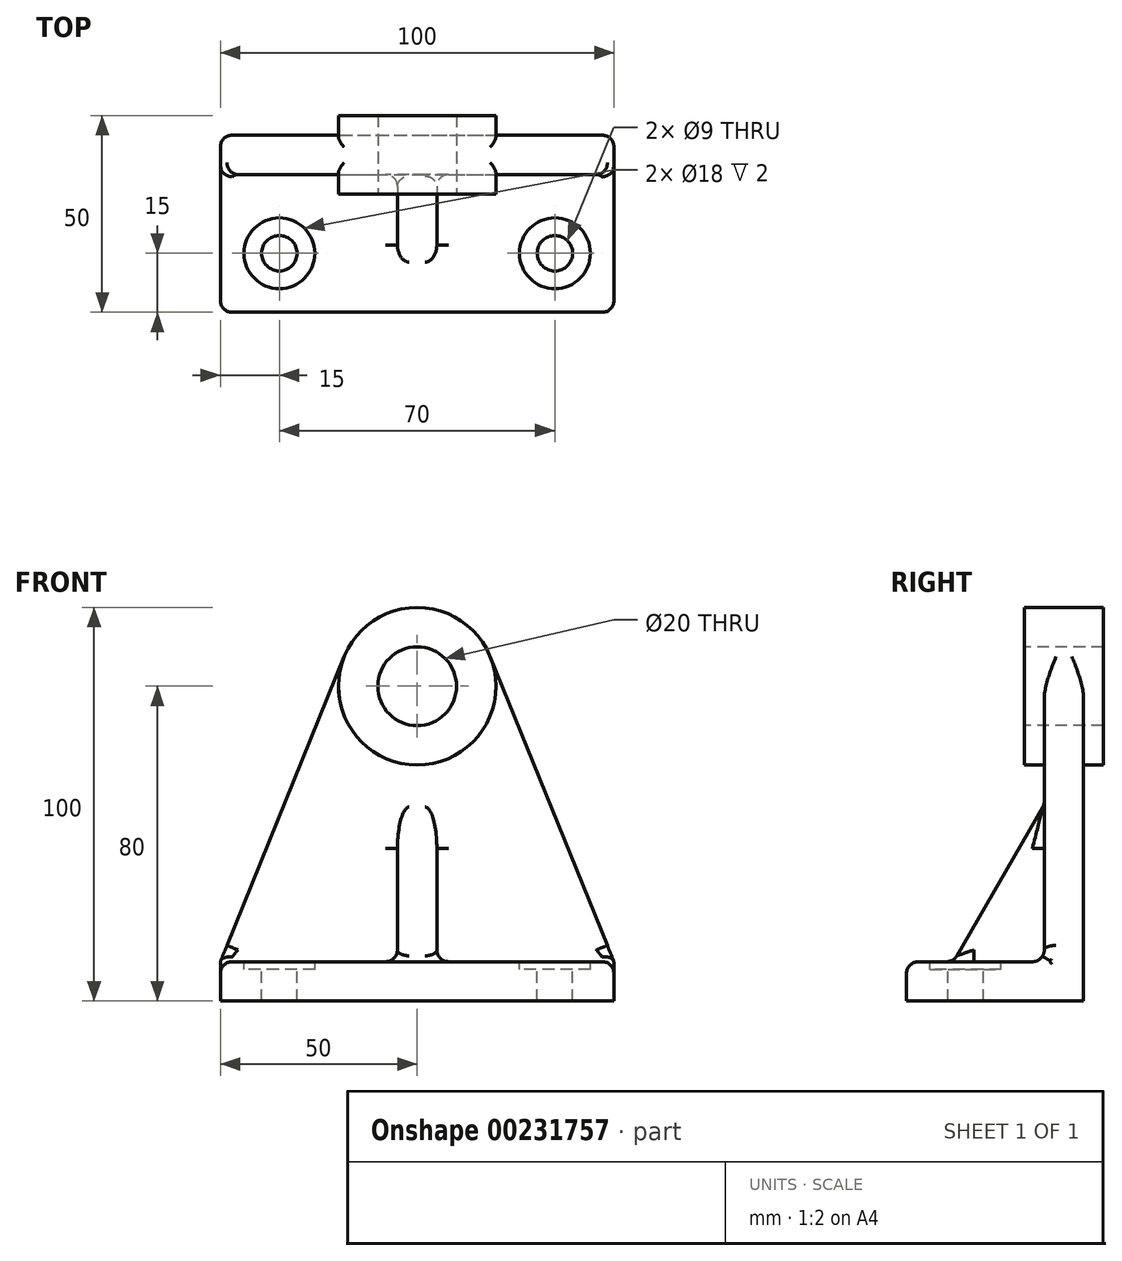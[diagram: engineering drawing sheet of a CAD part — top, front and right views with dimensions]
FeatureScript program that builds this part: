
annotation { "Feature Type Name" : "Feature", "Feature Type Description" : "" }
export const myFeature = defineFeature(function(context is Context, id is Id, definition is map)
    precondition{}
    {
        {
            var Q0;
            Q0=qCreatedBy(makeId("Front.planeOp"),FACE);
            var sketch = newSketch(context, id + "F0", { "sketchPlane" : qUnion([Q0])});
            skCircle(sketch, "E0", {"center": v(0, 80) * mm, "radius": 20 * mm, "construction": true});
            skLineSegment(sketch, "E1", {"start": v(-50, 0) * mm, "end": v(-50, 10) * mm});
            skLineSegment(sketch, "E2", {"start": v(-50, 10) * mm, "end": v(-18.53, 87.52) * mm});
            skLineSegment(sketch, "E3.MirrorCS", {"start": v(50, 10) * mm, "end": v(18.53, 87.52) * mm});
            skLineSegment(sketch, "E4.MirrorCS", {"start": v(50, 0) * mm, "end": v(50, 10) * mm});
            skLineSegment(sketch, "E5", {"start": v(-50, 0) * mm, "end": v(50, 0) * mm});
            skLineSegment(sketch, "E6", {"start": v(-18.53, 87.52) * mm, "end": v(18.53, 87.52) * mm});
            skSolve(sketch);
        }
        {
            var Q0;
            Q0 = qSketchRegion(id + "F0", true);
            extrude(context, id + "F1", {"entities" : qUnion([Q0]), "depth" : 45 * mm});
        }
        {
            var Q0;
            Q0=qCreatedBy(makeId("Right.planeOp"),FACE);
            var sketch = newSketch(context, id + "F2", { "sketchPlane" : qUnion([Q0])});
            skLineSegment(sketch, "E7.bottom", {"start": v(-55, 97.52) * mm, "end": v(-10, 97.52) * mm});
            skLineSegment(sketch, "E7.top", {"start": v(-55, 10) * mm, "end": v(-10, 10) * mm});
            skLineSegment(sketch, "E7.left", {"start": v(-55, 97.52) * mm, "end": v(-55, 10) * mm});
            skLineSegment(sketch, "E7.right", {"start": v(-10, 97.52) * mm, "end": v(-10, 10) * mm});
            skSolve(sketch);
        }
        {
            var Q0;
            Q0 = qSketchRegion(id + "F2", true);
            extrude(context, id + "F3", {"entities" : qUnion([Q0]), "operationType" : NewBodyOperationType.REMOVE, "endBound" : BoundingType.THROUGH_ALL, "oppositeDirection" : true, "depth" : 25 * mm, "hasSecondDirection" : true, "secondDirectionBound" : SecondDirectionBoundingType.THROUGH_ALL, "secondDirectionOppositeDirection" : false, "secondDirectionDepth" : 25 * mm});
        }
        {
            var Q0;
            Q0=qCreatedBy(makeId("Front.planeOp"),FACE);
            var sketch = newSketch(context, id + "F4", { "sketchPlane" : qUnion([Q0])});
            skCircle(sketch, "E8", {"center": v(0, 80) * mm, "radius": 20 * mm});
            skSolve(sketch);
        }
        {
            var Q0;
            Q0 = qSketchRegion(id + "F4", true);
            extrude(context, id + "F5", {"entities" : qUnion([Q0]), "operationType" : NewBodyOperationType.ADD, "depth" : 15 * mm, "hasSecondDirection" : true, "secondDirectionOppositeDirection" : true, "secondDirectionDepth" : 5 * mm});
        }
        {
            var Q0;
            Q0=qCreatedBy(makeId("Right.planeOp"),FACE);
            var sketch = newSketch(context, id + "F6", { "sketchPlane" : qUnion([Q0])});
            skLineSegment(sketch, "E9", {"start": v(-10, 50) * mm, "end": v(-33.1, 10) * mm});
            skLineSegment(sketch, "E10", {"start": v(-33.1, 10) * mm, "end": v(-33.1, 6) * mm});
            skLineSegment(sketch, "E11", {"start": v(-33.1, 6) * mm, "end": v(-6, 6) * mm});
            skLineSegment(sketch, "E12", {"start": v(-6, 6) * mm, "end": v(-6, 50) * mm});
            skLineSegment(sketch, "E13", {"start": v(-6, 50) * mm, "end": v(-10, 50) * mm});
            skSolve(sketch);
        }
        {
            var Q0;
            Q0 = qSketchRegion(id + "F6", true);
            extrude(context, id + "F7", {"entities" : qUnion([Q0]), "operationType" : NewBodyOperationType.ADD, "depth" : 5 * mm, "hasSecondDirection" : true, "secondDirectionOppositeDirection" : true, "secondDirectionDepth" : 5 * mm});
        }
        {
            var Q0;
            Q0=makeQuery(id+"F5.opExtrude","CAP_FACE",FACE,{"disambiguationData":[OSD([sQuery(id+"F4.wireOp",EDGE,"E8")])],"isStart":false});
            var sketch = newSketch(context, id + "F8", { "sketchPlane" : qUnion([Q0])});
            skCircle(sketch, "E14", {"center": v(0, 80) * mm, "radius": 10 * mm});
            skSolve(sketch);
        }
        {
            var Q0;
            Q0 = qSketchRegion(id + "F8", true);
            extrude(context, id + "F9", {"entities" : qUnion([Q0]), "operationType" : NewBodyOperationType.REMOVE, "endBound" : BoundingType.THROUGH_ALL, "oppositeDirection" : true, "depth" : 25 * mm});
        }
        {
            var Q0;
            Q0=makeQuery(id+"F3.boolean.opBoolean","COPY",FACE,{"derivedFrom":makeQuery(id+"F3.opExtrude","SWEPT_FACE",FACE,{"disambiguationData":[OSD([sQuery(id+"F2.wireOp",EDGE,"E7.top")])]})});
            var sketch = newSketch(context, id + "F10", { "sketchPlane" : qUnion([Q0])});
            skPoint(sketch, "E15", {"position": v(-35, -30) * mm});
            skPoint(sketch, "E16.MirrorP", {"position": v(35, -30) * mm});
            skSolve(sketch);
        }
        {
            var Q0;
            Q0=sQuery(id+"F10.wireOp",VERTEX,"E15");
            var Q1;
            Q1=sQuery(id+"F10.wireOp",VERTEX,"E16.MirrorP");
            var Q2;
            Q2=makeQuery(id+"F1.opExtrude","SWEPT_BODY",BODY,{"disambiguationData":[OSD([sQuery(id+"F0.wireOp",EDGE,"E1"),sQuery(id+"F0.wireOp",EDGE,"E2"),sQuery(id+"F0.wireOp",EDGE,"E3.MirrorCS"),sQuery(id+"F0.wireOp",EDGE,"E4.MirrorCS"),sQuery(id+"F0.wireOp",EDGE,"E5"),sQuery(id+"F0.wireOp",EDGE,"E6")])]});
            hole(context, id + "F11", {"style" : HoleStyle.C_BORE, "endStyle" : HoleEndStyle.THROUGH, "holeDiameter" : 9 * mm, "cBoreDiameter" : 18 * mm, "cBoreDepth" : 2 * mm, "locations" : qUnion([Q0, Q1]), "scope" : qUnion([Q2]), "isTappedThrough" : true});
        }
        {
            var Q0;
            Q0=makeQuery(id+"F1.opExtrude","CAP_EDGE",EDGE,{"disambiguationData":[OSD([sQuery(id+"F0.wireOp",EDGE,"E1")])],"isStart":false});
            var Q1;
            Q1=makeQuery(id+"F1.opExtrude","CAP_EDGE",EDGE,{"disambiguationData":[OSD([sQuery(id+"F0.wireOp",EDGE,"E4.MirrorCS")])],"isStart":false});
            fillet(context, id + "F12", {"entities" : qUnion([Q0, Q1]), "radius" : 3 * mm, "tangentPropagation" : true, "allowEdgeOverflow" : false});
        }
        {
            var Q0;
            Q0=makeQuery(id+"F7.opExtrude","CAP_EDGE",EDGE,{"disambiguationData":[OSD([sQuery(id+"F6.wireOp",EDGE,"E9")])],"isStart":false});
            var Q1;
            Q1=makeQuery(id+"F7.opExtrude","CAP_EDGE",EDGE,{"disambiguationData":[OSD([sQuery(id+"F6.wireOp",EDGE,"E9")])],"isStart":true});
            fillet(context, id + "F13", {"entities" : qUnion([Q0, Q1]), "radius" : 3 * mm, "tangentPropagation" : true, "allowEdgeOverflow" : false});
        }
        {
            var Q0;
            {var subQ0=sQuery(id+"F2.wireOp",EDGE,"E7.right");var subQ1=sQuery(id+"F2.wireOp",EDGE,"E7.top");Q0=makeQuery(id+"F7.boolean.opBoolean","SPLIT",EDGE,{"disambiguationData":[TD([makeQuery(id+"F1.opExtrude","SWEPT_FACE",FACE,{"disambiguationData":[OSD([sQuery(id+"F0.wireOp",EDGE,"E3.MirrorCS")])]})])],"derivedFrom":makeQuery(id+"F3.boolean.opBoolean","COPY",EDGE,{"derivedFrom":makeQuery(id+"F3.opExtrude","SWEPT_EDGE",EDGE,{"disambiguationData":[OSD([subQ1,subQ0])]})})});}
            var Q1;
            {var subQ0=sQuery(id+"F2.wireOp",EDGE,"E7.right");var subQ1=sQuery(id+"F2.wireOp",EDGE,"E7.top");Q1=makeQuery(id+"F7.boolean.opBoolean","SPLIT",EDGE,{"disambiguationData":[TD([makeQuery(id+"F1.opExtrude","SWEPT_FACE",FACE,{"disambiguationData":[OSD([sQuery(id+"F0.wireOp",EDGE,"E1")])]})])],"derivedFrom":makeQuery(id+"F3.boolean.opBoolean","COPY",EDGE,{"derivedFrom":makeQuery(id+"F3.opExtrude","SWEPT_EDGE",EDGE,{"disambiguationData":[OSD([subQ1,subQ0])]})})});}
            fillet(context, id + "F14", {"entities" : qUnion([Q0, Q1]), "radius" : 3 * mm, "tangentPropagation" : true, "allowEdgeOverflow" : false});
        }
        {
            var Q0;
            {var subQ0=sQuery(id+"F0.wireOp",EDGE,"E2");var subQ1=sQuery(id+"F0.wireOp",EDGE,"E1");Q0=makeQuery(id+"F3.boolean.opBoolean","SPLIT",EDGE,{"disambiguationData":[TD([makeQuery(id+"F1.opExtrude","CAP_FACE",FACE,{"disambiguationData":[OSD([subQ1,subQ0,sQuery(id+"F0.wireOp",EDGE,"E3.MirrorCS"),sQuery(id+"F0.wireOp",EDGE,"E4.MirrorCS"),sQuery(id+"F0.wireOp",EDGE,"E5"),sQuery(id+"F0.wireOp",EDGE,"E6")])],"isStart":true})])],"derivedFrom":makeQuery(id+"F1.opExtrude","SWEPT_EDGE",EDGE,{"disambiguationData":[OSD([subQ1,subQ0])]})});}
            var Q1;
            {var subQ0=sQuery(id+"F0.wireOp",EDGE,"E4.MirrorCS");var subQ1=sQuery(id+"F0.wireOp",EDGE,"E3.MirrorCS");Q1=makeQuery(id+"F3.boolean.opBoolean","SPLIT",EDGE,{"disambiguationData":[TD([makeQuery(id+"F1.opExtrude","CAP_FACE",FACE,{"disambiguationData":[OSD([sQuery(id+"F0.wireOp",EDGE,"E1"),sQuery(id+"F0.wireOp",EDGE,"E2"),subQ1,subQ0,sQuery(id+"F0.wireOp",EDGE,"E5"),sQuery(id+"F0.wireOp",EDGE,"E6")])],"isStart":true})])],"derivedFrom":makeQuery(id+"F1.opExtrude","SWEPT_EDGE",EDGE,{"disambiguationData":[OSD([subQ1,subQ0])]})});}
            fillet(context, id + "F15", {"entities" : qUnion([Q0, Q1]), "radius" : 3 * mm, "tangentPropagation" : true, "allowEdgeOverflow" : false});
        }
        {
            var Q0;
            Q0=makeQuery(id+"F3.boolean.opBoolean","INTERSECT",EDGE,{"derivedFrom":[makeQuery(id+"F1.opExtrude","CAP_FACE",FACE,{"disambiguationData":[OSD([sQuery(id+"F0.wireOp",EDGE,"E1"),sQuery(id+"F0.wireOp",EDGE,"E2"),sQuery(id+"F0.wireOp",EDGE,"E3.MirrorCS"),sQuery(id+"F0.wireOp",EDGE,"E4.MirrorCS"),sQuery(id+"F0.wireOp",EDGE,"E5"),sQuery(id+"F0.wireOp",EDGE,"E6")])],"isStart":false}),makeQuery(id+"F3.opExtrude","SWEPT_FACE",FACE,{"disambiguationData":[OSD([sQuery(id+"F2.wireOp",EDGE,"E7.top")])]})]});
            var Q1;
            Q1=makeQuery(id+"F3.boolean.opBoolean","INTERSECT",EDGE,{"derivedFrom":[makeQuery(id+"F1.opExtrude","SWEPT_FACE",FACE,{"disambiguationData":[OSD([sQuery(id+"F0.wireOp",EDGE,"E2")])]}),makeQuery(id+"F3.opExtrude","SWEPT_FACE",FACE,{"disambiguationData":[OSD([sQuery(id+"F2.wireOp",EDGE,"E7.right")])]})]});
            var Q2;
            Q2=makeQuery(id+"F3.boolean.opBoolean","INTERSECT",EDGE,{"derivedFrom":[makeQuery(id+"F1.opExtrude","SWEPT_FACE",FACE,{"disambiguationData":[OSD([sQuery(id+"F0.wireOp",EDGE,"E3.MirrorCS")])]}),makeQuery(id+"F3.opExtrude","SWEPT_FACE",FACE,{"disambiguationData":[OSD([sQuery(id+"F2.wireOp",EDGE,"E7.right")])]})]});
            var Q3;
            Q3=makeQuery(id+"F1.opExtrude","CAP_EDGE",EDGE,{"disambiguationData":[OSD([sQuery(id+"F0.wireOp",EDGE,"E3.MirrorCS")])],"isStart":true});
            var Q4;
            Q4=makeQuery(id+"F1.opExtrude","CAP_EDGE",EDGE,{"disambiguationData":[OSD([sQuery(id+"F0.wireOp",EDGE,"E2")])],"isStart":true});
            fillet(context, id + "F16", {"entities" : qUnion([Q0, Q1, Q2, Q3, Q4]), "radius" : 3 * mm, "tangentPropagation" : true, "allowEdgeOverflow" : false});
        }
        {
            var Q0;
            Q0=makeQuery(id+"F7.boolean.opBoolean","INTERSECT",EDGE,{"derivedFrom":[makeQuery(id+"F3.boolean.opBoolean","COPY",FACE,{"derivedFrom":makeQuery(id+"F3.opExtrude","SWEPT_FACE",FACE,{"disambiguationData":[OSD([sQuery(id+"F2.wireOp",EDGE,"E7.right")])]})}),makeQuery(id+"F7.opExtrude","CAP_FACE",FACE,{"disambiguationData":[OSD([sQuery(id+"F6.wireOp",EDGE,"E9"),sQuery(id+"F6.wireOp",EDGE,"E10"),sQuery(id+"F6.wireOp",EDGE,"E11"),sQuery(id+"F6.wireOp",EDGE,"E12"),sQuery(id+"F6.wireOp",EDGE,"E13")])],"isStart":false})]});
            fillet(context, id + "F17", {"entities" : qUnion([Q0]), "radius" : 3 * mm, "tangentPropagation" : true, "allowEdgeOverflow" : false});
        }
    });
